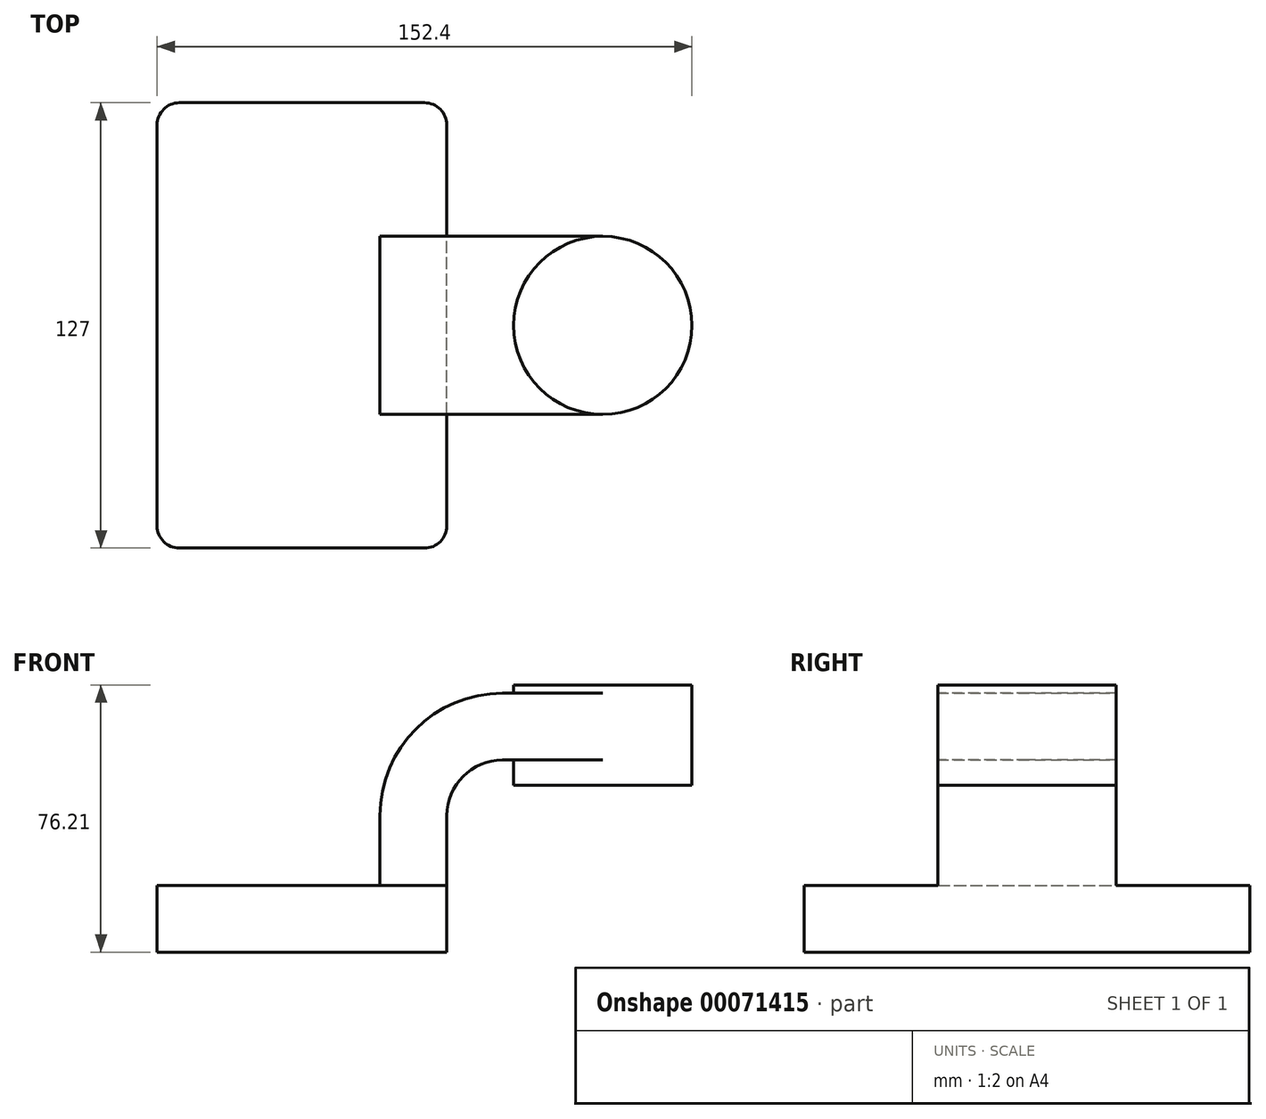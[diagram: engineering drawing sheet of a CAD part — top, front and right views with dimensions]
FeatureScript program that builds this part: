
annotation { "Feature Type Name" : "Feature", "Feature Type Description" : "" }
export const myFeature = defineFeature(function(context is Context, id is Id, definition is map)
    precondition{}
    {
        {
            var Q0;
            Q0=qCreatedBy(makeId("Front.planeOp"),FACE);
            var sketch = newSketch(context, id + "F0", { "sketchPlane" : qUnion([Q0])});
            skPoint(sketch, "E0.rect.middle", {"position": v(0, 0) * mm});
            skLineSegment(sketch, "E1.rect.bottom", {"start": v(60.33, 38.1) * mm, "end": v(111.12, 38.1) * mm});
            skLineSegment(sketch, "E1.rect.top", {"start": v(60.32, 66.68) * mm, "end": v(111.12, 66.68) * mm});
            skLineSegment(sketch, "E1.rect.left", {"start": v(60.33, 38.1) * mm, "end": v(60.32, 66.67) * mm});
            skLineSegment(sketch, "E1.rect.right", {"start": v(111.12, 38.1) * mm, "end": v(111.12, 66.67) * mm});
            skPoint(sketch, "E1.rect.middle", {"position": v(85.72, 52.39) * mm});
            skLineSegment(sketch, "E2.rect.bottom", {"start": v(-41.28, 9.52) * mm, "end": v(41.28, 9.52) * mm});
            skLineSegment(sketch, "E2.rect.top", {"start": v(-41.28, -9.53) * mm, "end": v(41.27, -9.53) * mm});
            skLineSegment(sketch, "E2.rect.left", {"start": v(-41.28, 9.52) * mm, "end": v(-41.28, -9.53) * mm});
            skLineSegment(sketch, "E2.rect.right", {"start": v(41.28, 9.52) * mm, "end": v(41.27, -9.53) * mm});
            skLineSegment(sketch, "E3", {"start": v(41.28, 9.52) * mm, "end": v(41.28, 29.37) * mm});
            skArc(sketch, "E4", {"start": v(41.27, 29.37) * mm, "mid": v(45.92, 40.6) * mm, "end": v(57.15, 45.25) * mm});
            skLineSegment(sketch, "E5", {"start": v(57.15, 45.25) * mm, "end": v(85.72, 45.25) * mm});
            skArc(sketch, "E6.1", {"start": v(22.23, 29.37) * mm, "mid": v(32.45, 54.07) * mm, "end": v(57.15, 64.3) * mm});
            skLineSegment(sketch, "E6.2", {"start": v(22.22, 9.52) * mm, "end": v(22.22, 29.37) * mm});
            skLineSegment(sketch, "E7", {"start": v(85.72, 38.1) * mm, "end": v(85.72, 66.68) * mm});
            skLineSegment(sketch, "E8", {"start": v(57.15, 64.3) * mm, "end": v(85.72, 64.3) * mm});
            skFitSpline(sketch, "E9", {"points": [v(-41.28, 9.52) * mm, v(57.15, 64.3) * mm], "startDerivative": vector(0, 91.63) * mm, "endDerivative": vector(120.5, 0) * mm});
            skSolve(sketch);
        }
        {
            var Q0;
            Q0=makeQuery(id+"F0.imprint","IMPRINT",FACE,{"disambiguationData":[TD([[makeQuery(id+"F0.imprint","IMPRINT",EDGE,{"derivedFrom":sQuery(id+"F0.wireOp",EDGE,"E2.rect.top")}),1.0]])]});
            extrude(context, id + "F1", {"entities" : qUnion([Q0]), "depth" : 127 * mm, "symmetric" : true});
        }
        {
            var Q0;
            {var subQ2=sQuery(id+"F0.wireOp",EDGE,"E3");Q0=makeQuery(id+"F0.imprint","IMPRINT",FACE,{"disambiguationData":[TD([[makeQuery(id+"F0.imprint","IMPRINT",EDGE,{"derivedFrom":subQ2}),1.0]])]});}
            var Q1;
            {var subQ0=sQuery(id+"F0.wireOp",EDGE,"E5");var subQ1=sQuery(id+"F0.wireOp",EDGE,"E1.rect.left");var subQ2=makeQuery(id+"F0.imprint","INTERSECT",VERTEX,{"derivedFrom":[subQ1,subQ0]});Q1=makeQuery(id+"F0.imprint","IMPRINT",FACE,{"disambiguationData":[TD([[makeQuery(id+"F0.imprint","IMPRINT",EDGE,{"disambiguationData":[TD([[subQ2,-1.0]])],"derivedFrom":subQ1}),-1.0]])]});}
            extrude(context, id + "F2", {"entities" : qUnion([Q0, Q1]), "operationType" : NewBodyOperationType.ADD, "depth" : 50.8 * mm, "symmetric" : true});
        }
        {
            var Q0;
            Q0=makeQuery(id+"F0.imprint","IMPRINT",FACE,{"disambiguationData":[TD([[makeQuery(id+"F0.imprint","IMPRINT",EDGE,{"derivedFrom":sQuery(id+"F0.wireOp",EDGE,"E6.1")}),1.0]])]});
            extrude(context, id + "F3", {"entities" : qUnion([Q0]), "operationType" : NewBodyOperationType.ADD, "depth" : 15.88 * mm, "symmetric" : true});
        }
        {
            var Q0;
            {var subQ4=sQuery(id+"F0.wireOp",EDGE,"E1.rect.right");Q0=makeQuery(id+"F0.imprint","IMPRINT",FACE,{"disambiguationData":[TD([[makeQuery(id+"F0.imprint","IMPRINT",EDGE,{"derivedFrom":subQ4}),1.0]])]});}
            var Q1;
            Q1=sQuery(id+"F0.wireOp",EDGE,"E7");
            revolve(context, id + "F4", {"operationType" : NewBodyOperationType.ADD, "entities" : qUnion([Q0]), "axis" : qUnion([Q1]), "revolveType" : RevolveType.FULL});
        }
        {
            var Q0;
            Q0=makeQuery(id+"F1.opExtrude","CAP_EDGE",EDGE,{"disambiguationData":[OSD([sQuery(id+"F0.wireOp",EDGE,"E2.rect.left")])],"isStart":false});
            var Q1;
            Q1=makeQuery(id+"F1.opExtrude","CAP_EDGE",EDGE,{"disambiguationData":[OSD([sQuery(id+"F0.wireOp",EDGE,"E2.rect.right")])],"isStart":false});
            var Q2;
            Q2=makeQuery(id+"F1.opExtrude","CAP_EDGE",EDGE,{"disambiguationData":[OSD([sQuery(id+"F0.wireOp",EDGE,"E2.rect.right")])],"isStart":true});
            var Q3;
            Q3=makeQuery(id+"F1.opExtrude","CAP_EDGE",EDGE,{"disambiguationData":[OSD([sQuery(id+"F0.wireOp",EDGE,"E2.rect.left")])],"isStart":true});
            fillet(context, id + "F5", {"entities" : qUnion([Q0, Q1, Q2, Q3]), "radius" : 6.35 * mm, "tangentPropagation" : true, "allowEdgeOverflow" : false});
        }
    });
